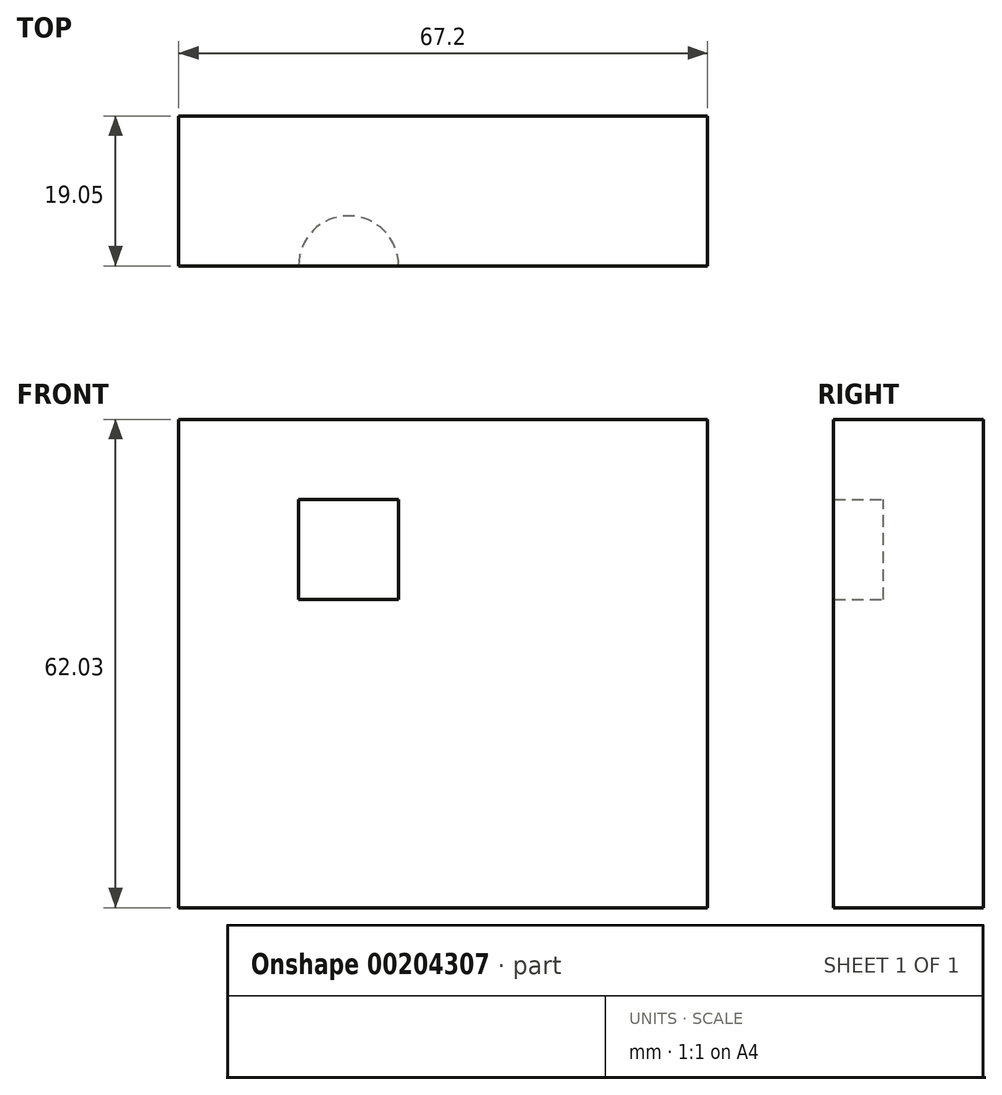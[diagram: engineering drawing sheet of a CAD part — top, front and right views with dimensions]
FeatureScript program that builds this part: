
annotation { "Feature Type Name" : "Feature", "Feature Type Description" : "" }
export const myFeature = defineFeature(function(context is Context, id is Id, definition is map)
    precondition{}
    {
        {
            var Q0;
            Q0=qCreatedBy(makeId("Front.planeOp"),FACE);
            var sketch = newSketch(context, id + "F2", { "sketchPlane" : qUnion([Q0])});
            skLineSegment(sketch, "E0.bottom", {"start": v(-30.84, 20.85) * mm, "end": v(36.36, 20.85) * mm});
            skLineSegment(sketch, "E0.top", {"start": v(-30.84, -41.18) * mm, "end": v(36.36, -41.18) * mm});
            skLineSegment(sketch, "E0.left", {"start": v(-30.84, 20.85) * mm, "end": v(-30.84, -41.18) * mm});
            skLineSegment(sketch, "E0.right", {"start": v(36.36, 20.85) * mm, "end": v(36.36, -41.18) * mm});
            skSolve(sketch);
        }
        {
            var Q0;
            Q0=makeQuery(id+"F2.imprint","IMPRINT",FACE,{"disambiguationData":[TD([[makeQuery(id+"F2.imprint","IMPRINT",EDGE,{"derivedFrom":sQuery(id+"F2.wireOp",EDGE,"E0.bottom")}),-1.0]])]});
            extrude(context, id + "F0", {"entities" : qUnion([Q0]), "depth" : 19.05 * mm});
        }
        {
            var Q0;
            Q0=makeQuery(id+"F0.opExtrude","CAP_FACE",FACE,{"disambiguationData":[OSD([sQuery(id+"F2.wireOp",EDGE,"E0.bottom"),sQuery(id+"F2.wireOp",EDGE,"E0.top"),sQuery(id+"F2.wireOp",EDGE,"E0.left"),sQuery(id+"F2.wireOp",EDGE,"E0.right")])],"isStart":false});
            var sketch = newSketch(context, id + "F1", { "sketchPlane" : qUnion([Q0])});
            skLineSegment(sketch, "E1.bottom", {"start": v(-9.25, -2.01) * mm, "end": v(-15.6, -2.01) * mm});
            skLineSegment(sketch, "E1.top", {"start": v(-9.25, 10.69) * mm, "end": v(-15.6, 10.69) * mm});
            skLineSegment(sketch, "E1.left", {"start": v(-9.25, -2.01) * mm, "end": v(-9.25, 10.69) * mm});
            skLineSegment(sketch, "E1.right", {"start": v(-15.6, -2.01) * mm, "end": v(-15.6, 10.69) * mm});
            skLineSegment(sketch, "E2", {"start": v(-15.6, 8.63) * mm, "end": v(-30.84, 8.63) * mm});
            skLineSegment(sketch, "E3", {"start": v(-12.43, 10.69) * mm, "end": v(-12.43, 20.85) * mm});
            skSolve(sketch);
        }
        {
            var Q0;
            {var subQ5=sQuery(id+"F1.wireOp",EDGE,"E1.bottom");Q0=makeQuery(id+"F1.imprint","IMPRINT",FACE,{"disambiguationData":[TD([[makeQuery(id+"F1.imprint","IMPRINT",EDGE,{"derivedFrom":subQ5}),-1.0]])]});}
            var Q1;
            Q1=sQuery(id+"F1.wireOp",EDGE,"E1.left");
            revolve(context, id + "F3", {"operationType" : NewBodyOperationType.REMOVE, "entities" : qUnion([Q0]), "axis" : qUnion([Q1]), "revolveType" : RevolveType.ONE_DIRECTION, "oppositeDirection" : true, "angle" : 180 * degree});
        }
    });
